# Revit family: QF_BPRO_SAW 2_572153
name_source: partatom
category: Sonderausstattung
revit_build: Autodesk Revit 2018 (Build: 20190510_1515(x64)
units: mm (PartAtom-declared; Revit-internal decimal feet)

## family parameters
Arbeitsebenenbasiert = Nein
Beim Laden mit Abzugskörper schneiden = Nein
Bemaßung runder Anschluss = Durchmesser verwenden
Gemeinsam genutzt = Nein
Immer vertikal = Ja
Raumberechnungspunkt = Nein
Teiletyp = Normal

## types (1)
- SAW 2
    3fach = Nein
    Artikel Nummer = 572153
    Beckenlänge = 305 mm  [stored 1.00066 ft]
    Beckentiefe = 200 mm  [stored 0.656168 ft]
    Beschreibung = Speisenausgabewagen;
2 Einzelbecken für 2x GN 1/1-200 oder deren Unterteilung;
mit Temperaturregler
    Beschreibung durch Hersteller analog Leistungsverzeichniskurztext = Abmessungen

Länge:					  936 mm
Breite:					  714 mm
Höhe:					  933 mm


Ausführung

Aufbau
Der Speisenausgabewagen besteht komplett aus CNS 18/10. Die Oberfläche ist mikroliert. Die fugenlos eingeschweißten, tiefgezogenen Warmhaltebecken sind nass oder trocken getrennt voneinander beheiz- und regelbar. In die einzelnen Becken ist eine Markierung geprägt, welche der Füllmenge von 4 Litern entspricht. Um die Becken läuft ein Profilrand. Die Nummerierung der Becken ist in die Abdeckung geprägt. Jedes der Becken ist extra mit einem Ablasshahn und einem Ablaufrohr versehen (gemeinsamer Ablauf unterhalb des Bodens). Die Absperrung befindet sich in Griffhöhe an der Längsseite, bedienbar mittels Drehschalter.
Das Bedienfeld liegt vertieft mit Ein/Aus-Schalter, Kontrollleuchte, Spiralkabel, Blindsteckerbuchse und Temperaturregler an der Stirnseite. Der Temperaturregler sichert die stufenlose Temperatureinstellung je Becken und Warmhaltefach.
Bedienseitig ist ein CNS-Sicherheits-Schiebegriff mit seitlichen Stoßschutzelementen aus Kunststoff (Polyamid) angebracht, welcher auch zum Schutz der Schalterelemente dient.
Fahrbar ist der Wagen mittels rostfreien Kunststoffrollen (2 Bockrollen und 2 Lenkrollen mit Feststeller mit 125 mm ø). Massive Stoßecken aus Kunststoff (Polyamid) an allen vier Ecken schützen vor Beschädigung.


Wagenkorpus
Der Wagenkorpus ist doppelwandig und isoliert.
Im Unterbau sind eingebaut:

zwei beheizte, fugenlose Schrankfächer mit je 6 Paar tiefgezogenen Auflagesicken im Abstand von 57,5 mm, zur Aufnahme von GN-Behältern der Größe GN 1/1 oder deren Unterteilungen. Die Schrankraumhöhe beträgt 350 mm. Die Flügeltüren sind doppelwandig und isoliert und um 270° schwenkbar. 
Die Schranktüren sind mit Griffmuscheln und einem selbsteinrastenden Verschluss versehen.


Zubehör/ Optionen

•	Klappbord an der Stirn- und/ oder den Längsseiten angebracht
•	Klappdeckel 1/3 zu 2/3, beide als Bord nutzbar
•	umlaufender Stoßschutz aus Kunststoff (Polyethylen)
•	Schiebedeckel mit Kugellagerführung
•	Hustenschutz aus ESG-Sicherheitsglas kundenseitig bis zur Abdeckung heruntergeführt oder kundenseitig mit einer Durchreichehöhe von 275 mm. Optional mit Wärmebord aus CNS (2 Keramikwärmestrahler à 250 W, 230 V, ungeregelt, gemeinsam mit dem jeweiligen Bain-Marie-Becken geschaltet.)
Länge Glasbord: 700 mm
Höhe inkl. Aufsatz: ca. 1325 mm
•	GN-Deckel-Ablage, zur Aufnahme von GN-Deckel 1/1 und deren Unterteilung, stirnseitig angebracht
•	Zugdeichsel links oder rechts
•	weitere Rollenausführungen siehe Gesamt-Preisliste


Technische Daten

Werkstoff:	CNS 18/10
Gewicht:		62 kg 
Kapazität:	2 Warmhaltebecken
		2 beheizte Schrankfächer
Warmhaltebecken:	für GN 1/1-200 oder deren Unterteilung
		Temperatur von +30°C bis +95 °C regelbar 
Schrankfächer:	für je 6 x GN1/1 mit 6 Paar Auflagesicken (Abstand 57,5mm); Hygieneausführung H1; Temperatur von +30°C bis +85°C regelbar
Anschlusswert:	220-240V / 50Hz / 1,9 kW


Besonderheit

•	Spritz- und strahlwassergeschützt (IPX 5)
•	VDE geprüft, GS-Zeichen
•	Abdeckung mit Profilrand
•	die Becken sind nass oder trocken beheizbar und können einzeln beheizt und geregelt werden
•	die Schrankfächer können unabhängig von den Becken beheizt werden.
•	Schrankfächer Hygieneausführung H1
•	geeignet für Optimierungsanlagen
•	gemäß DIN 18867, Teil 7 


Fabrikat

Hersteller:			B.PRO
Modell:				SAG 2
				B.PRO
    Beschreibung durch Hersteller analog Leistungsverzeichnislangtext = Abmessungen

Länge:					  936 mm
Länge (mit Option Schiebedeckel):	1006 mm
Breite:					  714 mm
Höhe:					  933 mm
Höhe (mit Option Schiebedeckel):	1000 mm


Ausführung

Aufbau
Der Speisenausgabewagen besteht komplett aus CNS 18/10. Die Oberfläche ist mikroliert. Die fugenlos eingeschweißten, tiefgezogenen Warmhaltebecken sind nass oder trocken getrennt voneinander beheiz- und regelbar. In die einzelnen Becken ist eine Markierung geprägt, welche der Füllmenge von 4 Litern entspricht. Um die Becken läuft ein Profilrand. Die Nummerierung der Becken ist in die Abdeckung geprägt. Die Becken sind an der Unterseite mit einem, gegen unbeabsichtigtes öffnen gesicherten, Ablasshahn ausgestattet.
Das Bedienfeld liegt vertieft mit Ein/Aus-Schalter, Kontrollleuchte und Temperaturregler an der Stirnseite. Der Temperaturregler sichert die stufenlose Temperatureinstellung je Becken. Ein Spiralkabel-anschluss mit einer Blindsteckerbuchse ist gegenüber der Bedienseite angebracht.
Bedienseitig ist ein CNS-Sicherheits-Schiebegriff mit seitlichen Stoßschutzelementen aus Kunststoff (Polyamid) angebracht, welcher auch zum Schutz der Schalterelemente dient.
Das offene Untergestell besitzt vier stabile Vierkantrohre, dazwischen eingeschweißt ein abgekantetes Ablagebord.
Fahrbar ist der Wagen mittels rostfreien Kunststoffrollen (4 Lenkrollen, davon 2 mit Feststeller mit 125 mm ø). Massive Stoßecken aus Kunststoff (Polyamid) an allen vier Ecken schützen vor Beschädigung.


Zubehör/ Optionen
•	Klappbord an der Stirn- und/ oder den Längsseiten angebracht
•	Klappdeckel 1/3 zu 2/3, beide als Bord nutzbar


•	Schiebedeckel mit Kugellagerführung
•	Hustenschutz aus ESG-Sicherheitsglas kundenseitig bis zur Abdeckung heruntergeführt oder kundenseitig mit einer Durchreichehöhe von 275 mm.
Optional mit Wärmebord aus CNS 
(2 Keramikwärmestrahler à 250 W, 230 V, ungeregelt, gemeinsam mit dem jeweiligen Bain-Marie-Becken geschaltet.)
Länge Glasbord: 700 mm
Höhe inkl. Aufsatz: ca. 1325 mm
•	GN-Deckel-Ablage, zur Aufnahme von GN-Deckel 1/1 und deren Unterteilung, stirnseitig angebracht
•	weitere Rollenausführungen siehe Gesamt-Preisliste
•	Arbeitshöhe (Oberkante Abdeckung) von 700 mm bis 899 mm konfigurierbar (Standard: 900 mm)


Technische Daten

Werkstoff:		CNS 18/10
Gewicht:		35,5 kg 
Kapazität:		2 Warmhaltebecken
Warmhaltebecken:	für GN 1/1-200 oder deren Unterteilung
		Temperatur von +30°C bis +95 °C regelbar 
Anschlusswert:		220-240V / 50Hz /1,4 kW


Besonderheit

•	Spritz- und strahlwassergeschützt (IPX 5)
•	Abdeckung mit Profilrand
•	die Becken sind nass oder trocken beheizbar
•	die Becken können einzeln beheizt und geregelt werden
•	Ablasshahn gegen unbeabsichtigtes Öffnen gesichert
•	geeignet für Optimierungsanlagen
•	gemäß DIN 18867, Teil 7



Fabrikat

Hersteller:			B.PRO
Modell:				SAW 2
				B.PRO
    CE Kennzeichnung = Ja
    Elektrische leistung = 1400 W
    Frequenz = 50 Hz
    Gerätegewicht Netto = 35.50 kg
    Großküchengerätezuordnung = Ja
    Hauptschalter integriert = Ja
    Hersteller = B.PRO GmbH
    Höhe = 933 mm  [stored 3.06102 ft]
    Höhe Arbeitsebene = 900 mm  [stored 2.95276 ft]
    Internetadresse Gerätehersteller = https://www.bpro-solutions.com
    Internetadresse für Ersatzteilliste = https://www.bpro-solutions.com
    Kosten = 1390.6 $
    Länge Gerätebreite = 931 mm
    Länge Korpus = 816 mm
    Material = QF_Metal-Stainless-Steel_general
    Material Dichtung = QF_Rubber-Black-Matt
    Material Kabel = QF_Rubber-Black-Matt
    Material Knöpfe1 = QF_Plastic-Black-Glossy
    Material Kunststoffteile = QF_Plastic-Black-Matt
    Material Metall glänzend = QF_Metal-Stainless-Steel_glossy
    Material Stoßschutz = QF_Rubber-Black-Matt
    Mittelabstand Schalter Strg = 46 mm
    Modell = SAW 2
    Schalldruckpegel = < 70 dB(A)
    Sockelhöhe = 168 mm  [stored 0.551181 ft]
    Spannung = 220 V
    Stecker System = Schuko Stecker
    Tiefe = 708 mm
    Tiefe Korpus = 630 mm
    Typenkommentare = Speisenausgabewagen, 2 Becken, 2 Schränke
    URL = https://www.bpro-solutions.com
    Versatz Becken Mitte Strg = 220 mm
    Warnhinweise = Wenn das Gerät nicht für die vorliegende Netzspannung oder Netzfrequenz ausgelegt ist, kann die Geräteelektrik zerstört werden. Vor dem Anschließen sicherstellen, dass die auf dem Typenschild angegebene Netzspannung und Netzfrequenz mit den entsprechenden Werten der Netzsteckdose übereinstimmen.

Spannungsrisse durch kaltes Wasser in heißen Bain-Marie-Becken. Wenn in heiße Bain-Marie-Becken kaltes Wasser gefüllt wird, kann der rasche Temperaturwechsel Spannungsrisse verursachen, die zu Korrosion führen können. Vor dem Befüllen mit kaltem Wasser Bain-Marie-Becken abkühlen lassen oder heiße Bain-Marie-Becken mit heißem Wasser befüllen.

Eingeklemmter Fuß. Beim Lösen und Arretieren der Feststellbremse kann der Fuß eingeklemmt und dabei verletzt werden. Darauf achten, dass der Fuß nicht zwischen die Feststellbremse und die Stoßecke gerät.

Heiße Bain-Marie-Becken / Heiße Geräteflächn / Heiße Gastronormbehälter. Im Warmhaltebetrieb können Gerätebecken, Geräteflächen und darin enthaltene Gastronormbehälter oder andere Gegenstände heiß werden und Verbrennungen verursachen. Heiße Teile nur geschützt (z.B. mit Topflappen oder Schutzhandschuhe) anfassen.

Heiße flüssige Speisen. Heiße flüssige Speisen können über den Rand des Gastronormbehälters fließen und Verbrühungen verursachen. Gastronormbehälter waagerecht halten. Gastronormbehälter stets mit Dichtungsdeckeln verschließen.

Heißes Wasser. Bei Nassbeschickung befindet sich im Bain-Marie-Becken nach Gebrauch heißes Wasser. Wenn das heiße Wasser abgelassen wird, besteht die Gefahr von Verbrühungen. Gerät vor Reinigung abkühlen lassen.

Ausführliche Gefahrenhinweise entnehmen Sie der Betriebsanleitung.
    Zubehör = Nein
    Zuleitung zum Gerät im Lieferumfang = Ja

note: [stored X ft] marks values corroborated as IEEE doubles in the binary element streams (Revit-internal decimal feet)
